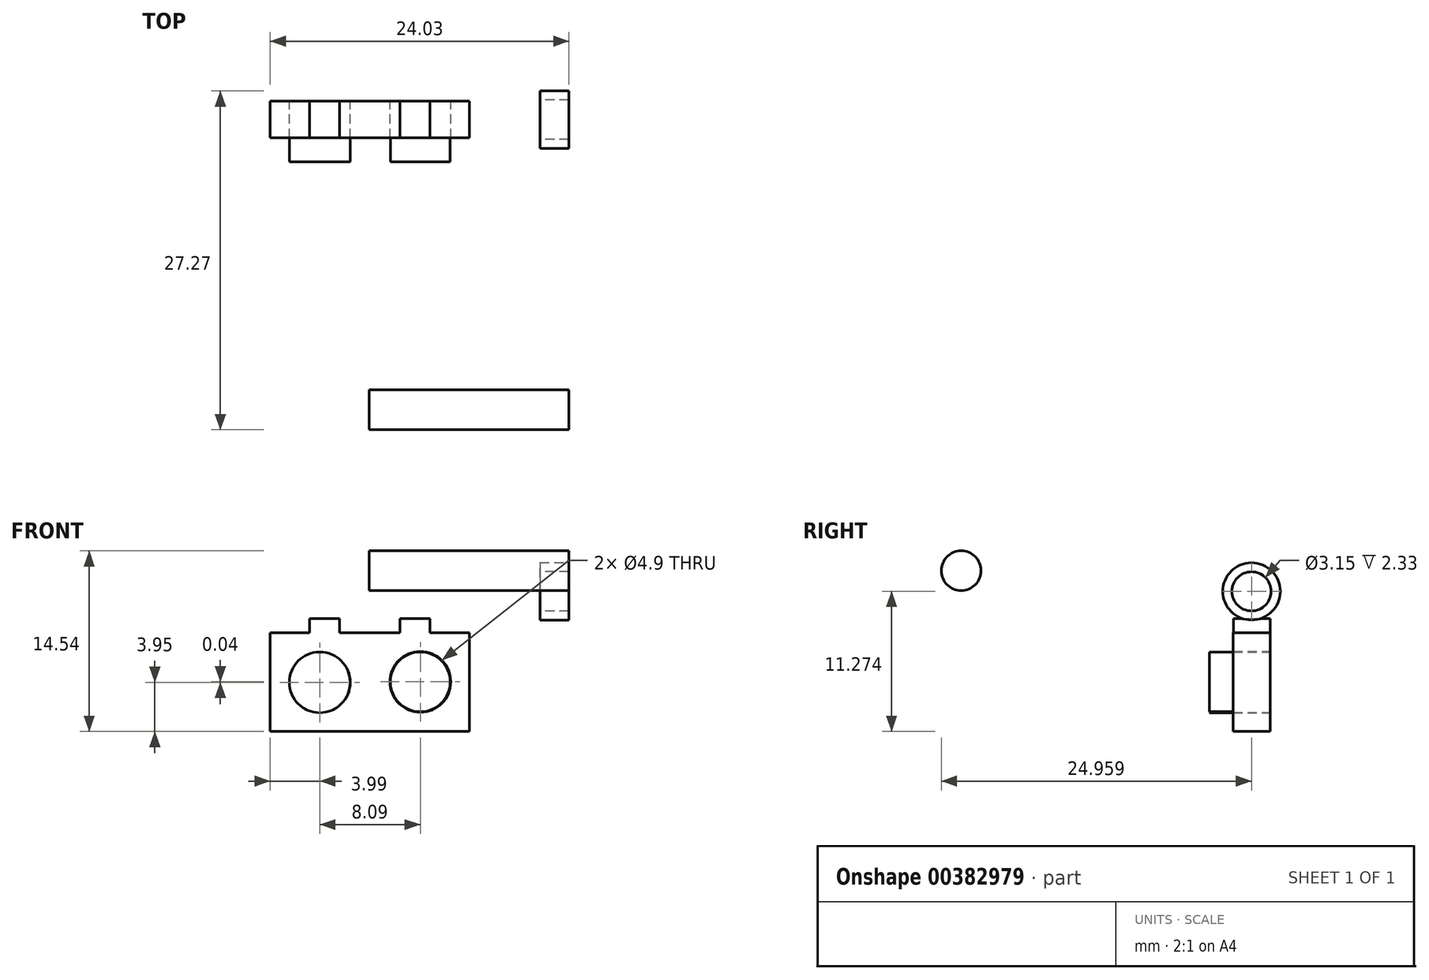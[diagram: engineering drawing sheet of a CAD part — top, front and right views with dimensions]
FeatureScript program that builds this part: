
annotation { "Feature Type Name" : "Feature", "Feature Type Description" : "" }
export const myFeature = defineFeature(function(context is Context, id is Id, definition is map)
    precondition{}
    {
        {
            var Q0;
            Q0=qCreatedBy(makeId("Front.planeOp"),FACE);
            var sketch = newSketch(context, id + "F0", { "sketchPlane" : qUnion([Q0])});
            skLineSegment(sketch, "E0", {"start": v(-8.01, 0) * mm, "end": v(-8.01, 7.94) * mm});
            skLineSegment(sketch, "E1", {"start": v(-8.01, 7.94) * mm, "end": v(-24.03, 7.94) * mm});
            skLineSegment(sketch, "E2", {"start": v(-24.03, 7.94) * mm, "end": v(-24.03, 0) * mm});
            skLineSegment(sketch, "E3", {"start": v(-24.03, 0) * mm, "end": v(-8.01, 0) * mm});
            skCircle(sketch, "E4", {"center": v(-20.04, 3.95) * mm, "radius": 2.45 * mm});
            skCircle(sketch, "E5", {"center": v(-11.95, 4) * mm, "radius": 2.45 * mm});
            skLineSegment(sketch, "E6", {"start": v(-20.85, 7.94) * mm, "end": v(-20.85, 9.07) * mm});
            skLineSegment(sketch, "E7", {"start": v(-20.85, 9.07) * mm, "end": v(-18.44, 9.07) * mm});
            skLineSegment(sketch, "E8", {"start": v(-18.44, 9.07) * mm, "end": v(-18.44, 7.94) * mm});
            skLineSegment(sketch, "E9", {"start": v(-18.44, 7.94) * mm, "end": v(-13.6, 7.94) * mm});
            skLineSegment(sketch, "E10", {"start": v(-13.6, 7.94) * mm, "end": v(-13.6, 9.07) * mm});
            skLineSegment(sketch, "E11", {"start": v(-13.6, 9.07) * mm, "end": v(-11.2, 9.07) * mm});
            skLineSegment(sketch, "E12", {"start": v(-11.2, 9.07) * mm, "end": v(-11.2, 7.94) * mm});
            skSolve(sketch);
        }
        {
            var Q0;
            {var subQ4=sQuery(id+"F0.wireOp",EDGE,"E0");Q0=makeQuery(id+"F0.imprint","IMPRINT",FACE,{"disambiguationData":[TD([[makeQuery(id+"F0.imprint","IMPRINT",EDGE,{"derivedFrom":subQ4}),1.0]])]});}
            extrude(context, id + "F1", {"entities" : qUnion([Q0]), "depth" : 2.96 * mm, "offsetDistance" : 25 * mm});
        }
        {
            var Q0;
            Q0=makeQuery(id+"F1.opExtrude","CAP_FACE",FACE,{"disambiguationData":[OSD([sQuery(id+"F0.wireOp",EDGE,"E0"),sQuery(id+"F0.wireOp",EDGE,"E1"),sQuery(id+"F0.wireOp",EDGE,"E2"),sQuery(id+"F0.wireOp",EDGE,"E3"),sQuery(id+"F0.wireOp",EDGE,"E4"),sQuery(id+"F0.wireOp",EDGE,"E5"),sQuery(id+"F0.wireOp",EDGE,"E9")])],"isStart":false});
            var sketch = newSketch(context, id + "F2", { "sketchPlane" : qUnion([Q0])});
            skCircle(sketch, "E13", {"center": v(-20.04, 3.95) * mm, "radius": 2.45 * mm});
            skCircle(sketch, "E14", {"center": v(-11.95, 4) * mm, "radius": 2.4 * mm});
            skSolve(sketch);
        }
        {
            var Q0;
            Q0=makeQuery(id+"F2.imprint","IMPRINT",FACE,{"disambiguationData":[TD([[makeQuery(id+"F2.imprint","IMPRINT",EDGE,{"derivedFrom":sQuery(id+"F2.wireOp",EDGE,"PouIKoqI-ImN8-zTDx-3qge-Od1ypUP8jgoV")}),1.0]])]});
            var Q1;
            Q1=makeQuery(id+"F2.imprint","IMPRINT",FACE,{"disambiguationData":[TD([[makeQuery(id+"F2.imprint","IMPRINT",EDGE,{"derivedFrom":sQuery(id+"F2.wireOp",EDGE,"E13")}),1.0]])]});
            extrude(context, id + "F3", {"entities" : qUnion([Q0, Q1]), "depth" : 1.92 * mm, "offsetDistance" : 25 * mm});
        }
        {
            var Q0;
            Q0=makeQuery(id+"F1.opExtrude","CAP_FACE",FACE,{"disambiguationData":[OSD([sQuery(id+"F0.wireOp",EDGE,"E0"),sQuery(id+"F0.wireOp",EDGE,"E1"),sQuery(id+"F0.wireOp",EDGE,"E2"),sQuery(id+"F0.wireOp",EDGE,"E3"),sQuery(id+"F0.wireOp",EDGE,"E4"),sQuery(id+"F0.wireOp",EDGE,"E5"),sQuery(id+"F0.wireOp",EDGE,"E9")])],"isStart":false});
            var sketch = newSketch(context, id + "F4", { "sketchPlane" : qUnion([Q0])});
            skCircle(sketch, "E15", {"center": v(-11.95, 4) * mm, "radius": 2.4 * mm});
            skSolve(sketch);
        }
        {
            var Q0;
            Q0=makeQuery(id+"F4.imprint","IMPRINT",FACE,{"disambiguationData":[TD([[makeQuery(id+"F4.imprint","IMPRINT",EDGE,{"derivedFrom":sQuery(id+"F4.wireOp",EDGE,"E15")}),1.0]])]});
            extrude(context, id + "F5", {"entities" : qUnion([Q0]), "depth" : 1.92 * mm, "offsetDistance" : 25 * mm});
        }
        {
            var Q0;
            {var subQ0=sQuery(id+"F0.wireOp",EDGE,"E6");Q0=makeQuery(id+"F0.imprint","IMPRINT",FACE,{"disambiguationData":[TD([[makeQuery(id+"F0.imprint","IMPRINT",EDGE,{"derivedFrom":subQ0}),-1.0]])]});}
            var Q1;
            {var subQ0=sQuery(id+"F0.wireOp",EDGE,"E10");Q1=makeQuery(id+"F0.imprint","IMPRINT",FACE,{"disambiguationData":[TD([[makeQuery(id+"F0.imprint","IMPRINT",EDGE,{"derivedFrom":subQ0}),-1.0]])]});}
            extrude(context, id + "F6", {"entities" : qUnion([Q0, Q1]), "operationType" : NewBodyOperationType.ADD, "depth" : 2.95 * mm, "offsetDistance" : 25 * mm});
        }
        {
            var Q0;
            Q0=qCreatedBy(makeId("Right.planeOp"),FACE);
            var sketch = newSketch(context, id + "F7", { "sketchPlane" : qUnion([Q0])});
            skCircle(sketch, "E16", {"center": v(-1.5, 11.27) * mm, "radius": 2.31 * mm});
            skSolve(sketch);
        }
        {
            var Q0;
            Q0=qSketchRegion(id+"F7",true);
            extrude(context, id + "F8", {"entities" : qUnion([Q0]), "oppositeDirection" : true, "depth" : 2.33 * mm, "offsetDistance" : 25 * mm});
        }
        {
            var Q0;
            Q0=makeQuery(id+"F8.opExtrude","CAP_FACE",FACE,{"disambiguationData":[OSD([sQuery(id+"F7.wireOp",EDGE,"E16")])],"isStart":false});
            var sketch = newSketch(context, id + "F9", { "sketchPlane" : qUnion([Q0])});
            skCircle(sketch, "E17", {"center": v(1.5, 11.27) * mm, "radius": 1.57 * mm});
            skSolve(sketch);
        }
        {
            var Q0;
            Q0=makeQuery(id+"F9.imprint","IMPRINT",FACE,{"disambiguationData":[TD([[makeQuery(id+"F9.imprint","IMPRINT",EDGE,{"derivedFrom":sQuery(id+"F9.wireOp",EDGE,"E17")}),1.0]])]});
            extrude(context, id + "F10", {"entities" : qUnion([Q0]), "operationType" : NewBodyOperationType.REMOVE, "oppositeDirection" : true, "depth" : 25 * mm, "offsetDistance" : 25 * mm});
        }
        {
            var Q0;
            Q0=qCreatedBy(makeId("Right.planeOp"),FACE);
            var sketch = newSketch(context, id + "F11", { "sketchPlane" : qUnion([Q0])});
            skCircle(sketch, "E18", {"center": v(-24.85, 12.94) * mm, "radius": 1.6 * mm});
            skSolve(sketch);
        }
        {
            var Q0;
            Q0=makeQuery(id+"F11.imprint","IMPRINT",FACE,{"disambiguationData":[TD([[makeQuery(id+"F11.imprint","IMPRINT",EDGE,{"derivedFrom":sQuery(id+"F11.wireOp",EDGE,"E18")}),1.0]])]});
            extrude(context, id + "F12", {"entities" : qUnion([Q0]), "oppositeDirection" : true, "depth" : 16.08 * mm, "offsetDistance" : 25 * mm});
        }
    });
